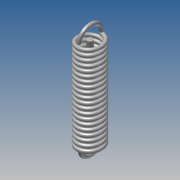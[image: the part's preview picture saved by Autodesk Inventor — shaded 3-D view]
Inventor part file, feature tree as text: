
AUTODESK INVENTOR PART (.ipt)
format: ipt  version: 2014 SP1 (Build 180222100, 222)  size: 1,518,592 bytes
history: native  units: in
note: dims shown in document units (in); Inventor stores cm internally (conversion verified against a paired STEP export)
features: sketch x8, plane x2, revolve x2, extrude x2, helix x1
ambient origin geometry x8: Origin, YZ Plane, XZ Plane, XY Plane, X Axis, Y Axis, Z Axis, Center Point
bodies: Solid1 (feature_tree)
feature tree (15):
  helix  "Coil1"  [1 undecoded]
  sketch  "Sketch11"  dims[d19=180.0deg d20=0.2in]
  plane  "Work Plane1"
  revolve  "Revolution1"  [1 undecoded]
  sketch  "Sketch14"  dims[d24=0.3in d25=5.0in d26=0.0in]
  plane  "Work Plane2"
  extrude  "Extrusion2"  Depth=0.2in
  revolve  "Revolution2"  Angle=180.0deg
  extrude  "Extrusion3"  Depth=5.0in TaperAngle=0.0deg
  sketch  "Sketch1"  dims[d2=0.6in]
  sketch  "Sketch3"  dims[d3=0.25in d4=1.0in d5=7.874in d6=0.0in d7=90.0deg d8=90.0deg d9=0.0in d10=0.0in d18=0.2in]
  sketch  "Sketch12"  dims[d21=0.02in d22=0.0in d23=180.0deg]
  sketch  "Sketch15"
  sketch  "Sketch17"
  sketch  "Sketch18"
note: 2 required parameter values undecoded (feature->parameter linkage not recoverable at this tier; creation-order binding heuristic only, values carry confidence <= 0.55)